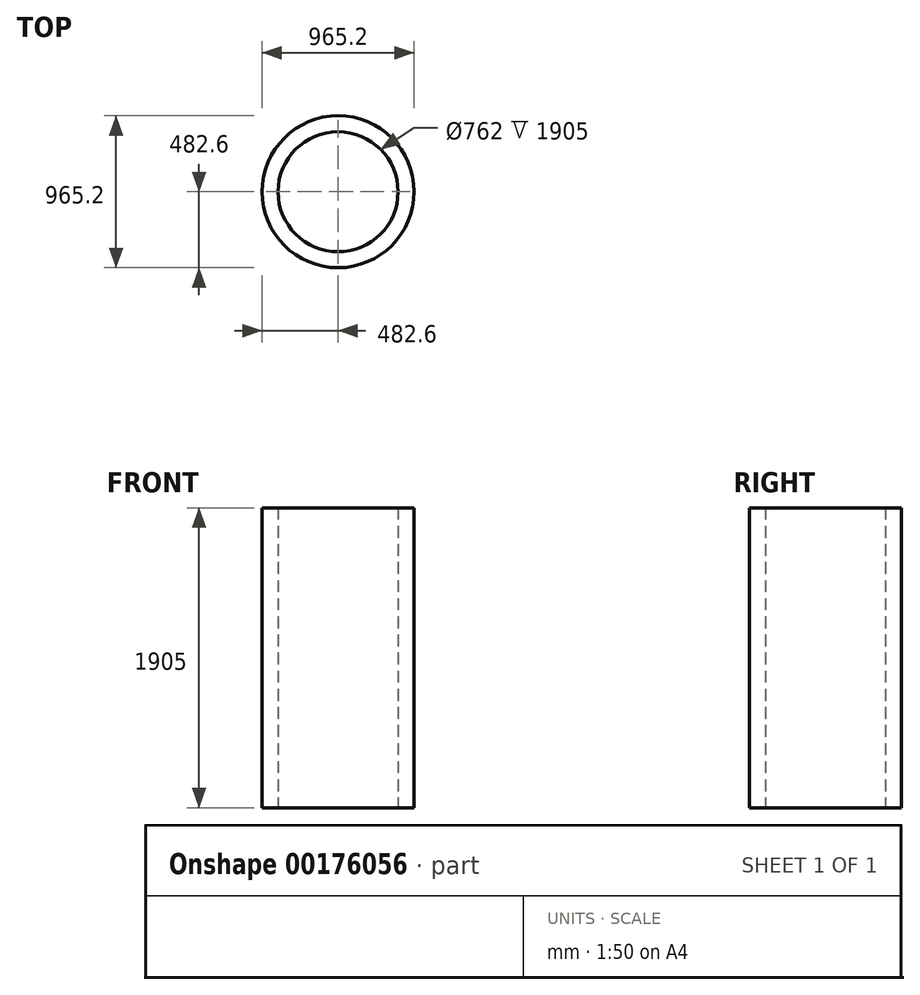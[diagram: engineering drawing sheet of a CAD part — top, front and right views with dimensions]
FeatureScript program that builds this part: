
annotation { "Feature Type Name" : "Feature", "Feature Type Description" : "" }
export const myFeature = defineFeature(function(context is Context, id is Id, definition is map)
    precondition{}
    {
        {
            var Q0;
            Q0=qCreatedBy(makeId("Top.planeOp"),FACE);
            var sketch = newSketch(context, id + "F0", { "sketchPlane" : qUnion([Q0])});
            skCircle(sketch, "E0", {"center": v(0, 0) * mm, "radius": 482.6 * mm});
            skCircle(sketch, "E1", {"center": v(0, 0) * mm, "radius": 381 * mm});
            skSolve(sketch);
        }
        {
            var Q0;
            Q0=makeQuery(id+"F0.imprint","IMPRINT",FACE,{"disambiguationData":[TD([[makeQuery(id+"F0.imprint","IMPRINT",EDGE,{"derivedFrom":sQuery(id+"F0.wireOp",EDGE,"E0")}),1.0]])]});
            extrude(context, id + "F1", {"entities" : qUnion([Q0]), "depth" : 1905 * mm});
        }
    });
